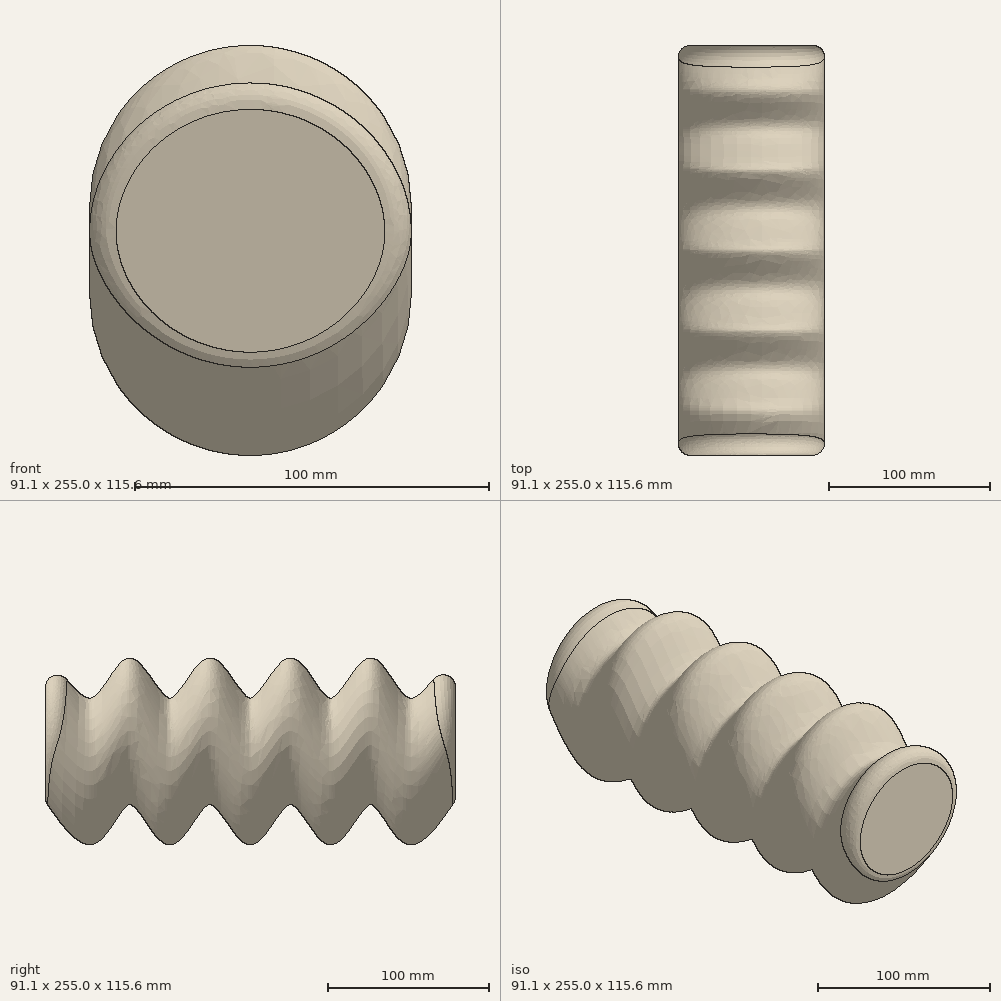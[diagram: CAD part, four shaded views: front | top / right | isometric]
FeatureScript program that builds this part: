
annotation { "Feature Type Name" : "Feature", "Feature Type Description" : "" }
export const myFeature = defineFeature(function(context is Context, id is Id, definition is map)
    precondition{}
    {
        {
            var Q0;
            Q0=qCreatedBy(makeId("Front.planeOp"),FACE);
            var sketch = newSketch(context, id + "F0", { "sketchPlane" : qUnion([Q0])});
            skCircle(sketch, "E0", {"center": v(0, 0) * mm, "radius": 43.06 * mm});
            skPoint(sketch, "E1", {"position": v(0, -43.06) * mm});
            skSolve(sketch);
        }
        {
            var Q0;
            Q0=qCreatedBy(makeId("Front.planeOp"),FACE);
            cPlane(context, id + "F1", {"entities" : qUnion([Q0]), "cplaneType" : CPlaneType.OFFSET, "offset" : 250 * mm, "width" : 150 * mm, "height" : 150 * mm});
        }
        {
            var Q0;
            Q0=qCreatedBy(id+"F1.planeOp",FACE);
            var sketch = newSketch(context, id + "F2", { "sketchPlane" : qUnion([Q0])});
            skCircle(sketch, "E2", {"center": v(0, 0) * mm, "radius": 43.06 * mm});
            skPoint(sketch, "E3", {"position": v(0, -43.06) * mm});
            skSolve(sketch);
        }
        {
            var Q0;
            Q0=qCreatedBy(makeId("Right.planeOp"),FACE);
            var sketch = newSketch(context, id + "F3", { "sketchPlane" : qUnion([Q0])});
            skPoint(sketch, "E4.0", {"position": v(-250, -43.06) * mm});
            skPoint(sketch, "E5.0", {"position": v(0, -43.06) * mm});
            skLineSegment(sketch, "E6", {"start": v(-250, -43.06) * mm, "end": v(0, -43.06) * mm, "construction": true});
            skFitSpline(sketch, "E7", {"points": [v(-250, -43.06) * mm, v(-225, -68.06) * mm, v(-200, -43.06) * mm, v(-175, -68.06) * mm, v(-150, -43.06) * mm, v(-125, -68.06) * mm, v(-100, -43.06) * mm, v(-75, -68.06) * mm, v(-50, -43.06) * mm, v(-25, -68.06) * mm, v(0, -43.06) * mm], "startDerivative": vector(24.26, 0) * mm, "endDerivative": vector(40.13, 0) * mm});
            skSolve(sketch);
        }
        {
            var Q0;
            Q0=qCreatedBy(makeId("Right.planeOp"),FACE);
            var sketch = newSketch(context, id + "F4", { "sketchPlane" : qUnion([Q0])});
            skLineSegment(sketch, "E8.0", {"start": v(-250, -43.06) * mm, "end": v(0, -43.06) * mm});
            skSolve(sketch);
        }
        {
            var Q0;
            Q0=makeQuery(id+"F2.imprint","IMPRINT",FACE,{"disambiguationData":[TD([[makeQuery(id+"F2.imprint","IMPRINT",EDGE,{"derivedFrom":sQuery(id+"F2.wireOp",EDGE,"E2")}),1.0]])]});
            var Q1;
            Q1=makeQuery(id+"F0.imprint","IMPRINT",FACE,{"disambiguationData":[TD([[makeQuery(id+"F0.imprint","IMPRINT",EDGE,{"derivedFrom":sQuery(id+"F0.wireOp",EDGE,"E0")}),1.0]])]});
            var Q2;
            Q2=sQuery(id+"F3.wireOp",EDGE,"E7");
            var Q3;
            Q3=sQuery(id+"FqDemqZTmZ8Oy63_0.2.F4.wireOp",EDGE,"E8.0");
            var Q4;
            Q4=sQuery(id+"FqDemqZTmZ8Oy63_0.1.F4.wireOp",EDGE,"E8.0");
            var Q5;
            Q5=sQuery(id+"FqDemqZTmZ8Oy63_0.3.F4.wireOp",EDGE,"E8.0");
            loft(context, id + "F5", {"addGuides" : true, "sheetProfilesArray" : [{ "sheetProfileEntities" : qUnion([Q0]) }, { "sheetProfileEntities" : qUnion([Q1]) }], "guidesArray" : [{ "guideEntities" : qUnion([Q2]), "guideDerivativeType" : LoftGuideDerivativeType.DEFAULT, "guideDerivativeMagnitude" : 1 }, { "guideEntities" : qUnion([Q3]), "guideDerivativeType" : LoftGuideDerivativeType.DEFAULT, "guideDerivativeMagnitude" : 1 }, { "guideEntities" : qUnion([Q4]), "guideDerivativeType" : LoftGuideDerivativeType.DEFAULT, "guideDerivativeMagnitude" : 1 }, { "guideEntities" : qUnion([Q5]), "guideDerivativeType" : LoftGuideDerivativeType.DEFAULT, "guideDerivativeMagnitude" : 1 }]});
        }
        {
            var Q0;
            Q0=makeQuery(id+"F5.opLoft","MID_CAP_EDGE",EDGE,{"disambiguationData":[OSD([sQuery(id+"F2.wireOp",EDGE,"E2"),sQuery(id+"FqDemqZTmZ8Oy63_0.2.F4.wireOp",EDGE,"E8.0"),sQuery(id+"FqDemqZTmZ8Oy63_0.3.F4.wireOp",EDGE,"E8.0")])],"capPos":0.0});
            var Q1;
            Q1=makeQuery(id+"F5.opLoft","MID_CAP_EDGE",EDGE,{"disambiguationData":[OSD([sQuery(id+"F0.wireOp",EDGE,"E0"),sQuery(id+"F3.wireOp",EDGE,"E7"),sQuery(id+"FqDemqZTmZ8Oy63_0.3.F4.wireOp",EDGE,"E8.0")])],"capPos":1.0});
            fillet(context, id + "F6", {"entities" : qUnion([Q0, Q1]), "radius" : 5 * mm, "tangentPropagation" : true, "allowEdgeOverflow" : false});
        }
        {
            var Q0;
            Q0=makeQuery(id+"F5.opLoft","CAP_FACE",FACE,{"disambiguationData":[OSD([makeQuery(id+"F0.imprint","IMPRINT",FACE,{"disambiguationData":[TD([[makeQuery(id+"F0.imprint","IMPRINT",EDGE,{"derivedFrom":sQuery(id+"F0.wireOp",EDGE,"E0")}),1.0]])]})])],"isStart":true});
            shell(context, id + "F7", {"entities" : qUnion([Q0]), "thickness" : 2.5 * mm, "oppositeDirection" : true});
        }
    });
